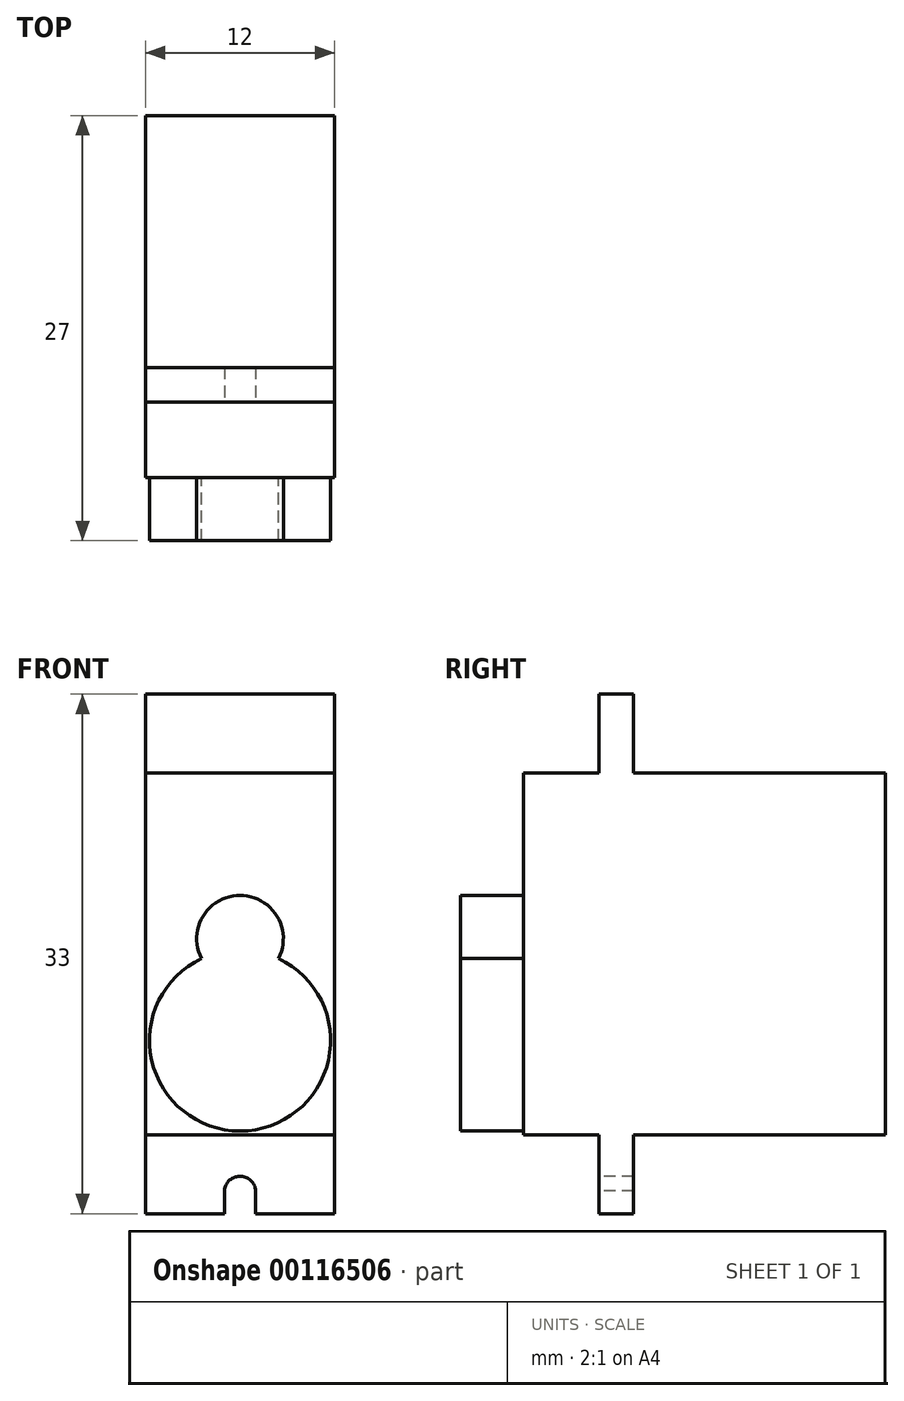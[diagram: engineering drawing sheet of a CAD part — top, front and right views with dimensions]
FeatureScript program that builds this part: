
annotation { "Feature Type Name" : "Feature", "Feature Type Description" : "" }
export const myFeature = defineFeature(function(context is Context, id is Id, definition is map)
    precondition{}
    {
        {
            var Q0;
            Q0=qCreatedBy(makeId("Front.planeOp"),FACE);
            var sketch = newSketch(context, id + "F0", { "sketchPlane" : qUnion([Q0])});
            skLineSegment(sketch, "E0.bottom", {"start": v(0, 0) * mm, "end": v(12, 0) * mm});
            skLineSegment(sketch, "E0.top", {"start": v(0, -23) * mm, "end": v(12, -23) * mm});
            skLineSegment(sketch, "E0.left", {"start": v(0, 0) * mm, "end": v(0, -23) * mm});
            skLineSegment(sketch, "E0.right", {"start": v(12, 0) * mm, "end": v(12, -23) * mm});
            skSolve(sketch);
        }
        {
            var Q0;
            Q0=makeQuery(id+"F0.imprint","IMPRINT",FACE,{"disambiguationData":[TD([[makeQuery(id+"F0.imprint","IMPRINT",EDGE,{"derivedFrom":sQuery(id+"F0.wireOp",EDGE,"E0.bottom")}),-1.0]])]});
            extrude(context, id + "F1", {"entities" : qUnion([Q0]), "depth" : 23 * mm});
        }
        {
            var Q0;
            Q0=makeQuery(id+"F1.opExtrude","CAP_FACE",FACE,{"disambiguationData":[OSD([sQuery(id+"F0.wireOp",EDGE,"E0.bottom"),sQuery(id+"F0.wireOp",EDGE,"E0.top"),sQuery(id+"F0.wireOp",EDGE,"E0.left"),sQuery(id+"F0.wireOp",EDGE,"E0.right")])],"isStart":false});
            var sketch = newSketch(context, id + "F2", { "sketchPlane" : qUnion([Q0])});
            skCircle(sketch, "E1", {"center": v(6, -17) * mm, "radius": 5.75 * mm});
            skCircle(sketch, "E2", {"center": v(6, -10.53) * mm, "radius": 2.75 * mm});
            skSolve(sketch);
        }
        {
            var Q0;
            {var subQ0=sQuery(id+"F2.wireOp",EDGE,"E2");var subQ1=sQuery(id+"F2.wireOp",EDGE,"E1");var subQ2=makeQuery(id+"F2.imprint","INTERSECT",VERTEX,{"disambiguationData":[OD(0.0)],"derivedFrom":[subQ1,subQ0]});Q0=makeQuery(id+"F2.imprint","IMPRINT",FACE,{"disambiguationData":[TD([[makeQuery(id+"F2.imprint","IMPRINT",EDGE,{"disambiguationData":[TD([[subQ2,1.0]])],"derivedFrom":subQ1}),-1.0]])]});}
            var Q1;
            {var subQ0=sQuery(id+"F2.wireOp",EDGE,"E2");var subQ1=sQuery(id+"F2.wireOp",EDGE,"E1");var subQ2=makeQuery(id+"F2.imprint","INTERSECT",VERTEX,{"disambiguationData":[OD(0.0)],"derivedFrom":[subQ1,subQ0]});Q1=makeQuery(id+"F2.imprint","IMPRINT",FACE,{"disambiguationData":[TD([[makeQuery(id+"F2.imprint","IMPRINT",EDGE,{"disambiguationData":[TD([[subQ2,1.0]])],"derivedFrom":subQ1}),1.0]])]});}
            var Q2;
            {var subQ0=sQuery(id+"F2.wireOp",EDGE,"E2");var subQ1=sQuery(id+"F2.wireOp",EDGE,"E1");var subQ2=makeQuery(id+"F2.imprint","INTERSECT",VERTEX,{"disambiguationData":[OD(0.0)],"derivedFrom":[subQ1,subQ0]});Q2=makeQuery(id+"F2.imprint","IMPRINT",FACE,{"disambiguationData":[TD([[makeQuery(id+"F2.imprint","IMPRINT",EDGE,{"disambiguationData":[TD([[subQ2,-1.0]])],"derivedFrom":subQ1}),1.0]])]});}
            extrude(context, id + "F3", {"entities" : qUnion([Q0, Q1, Q2]), "operationType" : NewBodyOperationType.ADD, "depth" : 4 * mm});
        }
        {
            var Q0;
            Q0=makeQuery(id+"F1.opExtrude","SWEPT_FACE",FACE,{"disambiguationData":[OSD([sQuery(id+"F0.wireOp",EDGE,"E0.bottom")])]});
            var sketch = newSketch(context, id + "F4", { "sketchPlane" : qUnion([Q0])});
            skLineSegment(sketch, "E3.bottom", {"start": v(0, -16) * mm, "end": v(12, -16) * mm});
            skLineSegment(sketch, "E3.top", {"start": v(0, -18.2) * mm, "end": v(12, -18.2) * mm});
            skLineSegment(sketch, "E3.left", {"start": v(0, -16) * mm, "end": v(0, -18.2) * mm});
            skLineSegment(sketch, "E3.right", {"start": v(12, -16) * mm, "end": v(12, -18.2) * mm});
            skSolve(sketch);
        }
        {
            var Q0;
            Q0=makeQuery(id+"F4.imprint","IMPRINT",FACE,{"disambiguationData":[TD([[makeQuery(id+"F4.imprint","IMPRINT",EDGE,{"derivedFrom":sQuery(id+"F4.wireOp",EDGE,"E3.bottom")}),-1.0]])]});
            extrude(context, id + "F5", {"entities" : qUnion([Q0]), "operationType" : NewBodyOperationType.ADD, "depth" : 5 * mm});
        }
        {
            var Q0;
            Q0=makeQuery(id+"F4.imprint","IMPRINT",FACE,{"disambiguationData":[TD([[makeQuery(id+"F4.imprint","IMPRINT",EDGE,{"derivedFrom":sQuery(id+"F4.wireOp",EDGE,"E3.bottom")}),-1.0]])]});
            extrude(context, id + "F6", {"entities" : qUnion([Q0]), "operationType" : NewBodyOperationType.ADD, "oppositeDirection" : true, "depth" : 28 * mm});
        }
        {
            var Q0;
            Q0=makeQuery(id+"F6.opExtrude","SWEPT_FACE",FACE,{"disambiguationData":[OSD([sQuery(id+"F4.wireOp",EDGE,"E3.top")])]});
            var sketch = newSketch(context, id + "F7", { "sketchPlane" : qUnion([Q0])});
            skLineSegment(sketch, "E4", {"start": v(6, -28) * mm, "end": v(6, 5.45) * mm, "construction": true});
            skArc(sketch, "E5", {"start": v(7, -26.68) * mm, "mid": v(6.02, -25.62) * mm, "end": v(5, -26.63) * mm});
            skLineSegment(sketch, "E6", {"start": v(5, -26.63) * mm, "end": v(5.04, -29.42) * mm});
            skLineSegment(sketch, "E7", {"start": v(7, -26.57) * mm, "end": v(7, -29.57) * mm});
            skLineSegment(sketch, "E8", {"start": v(7, -29.57) * mm, "end": v(5.04, -29.42) * mm});
            skSolve(sketch);
        }
        {
            var Q0;
            {var subQ1=sQuery(id+"F7.wireOp",EDGE,"E5");var subQ5=sQuery(id+"F7.wireOp",EDGE,"E6");var subQ6=makeQuery(id+"F7.imprint","INTERSECT",VERTEX,{"derivedFrom":[subQ1,subQ5]});Q0=makeQuery(id+"F7.imprint","IMPRINT",FACE,{"disambiguationData":[TD([[makeQuery(id+"F7.imprint","IMPRINT",EDGE,{"disambiguationData":[TD([[subQ6,1.0]])],"derivedFrom":subQ1}),1.0]])]});}
            var Q1;
            {var subQ0=sQuery(id+"F7.wireOp",EDGE,"E8");Q1=makeQuery(id+"F7.imprint","IMPRINT",FACE,{"disambiguationData":[TD([[makeQuery(id+"F7.imprint","IMPRINT",EDGE,{"derivedFrom":subQ0}),-1.0]])]});}
            extrude(context, id + "F8", {"entities" : qUnion([Q0, Q1]), "operationType" : NewBodyOperationType.REMOVE, "oppositeDirection" : true, "depth" : 4.37 * mm});
        }
    });
